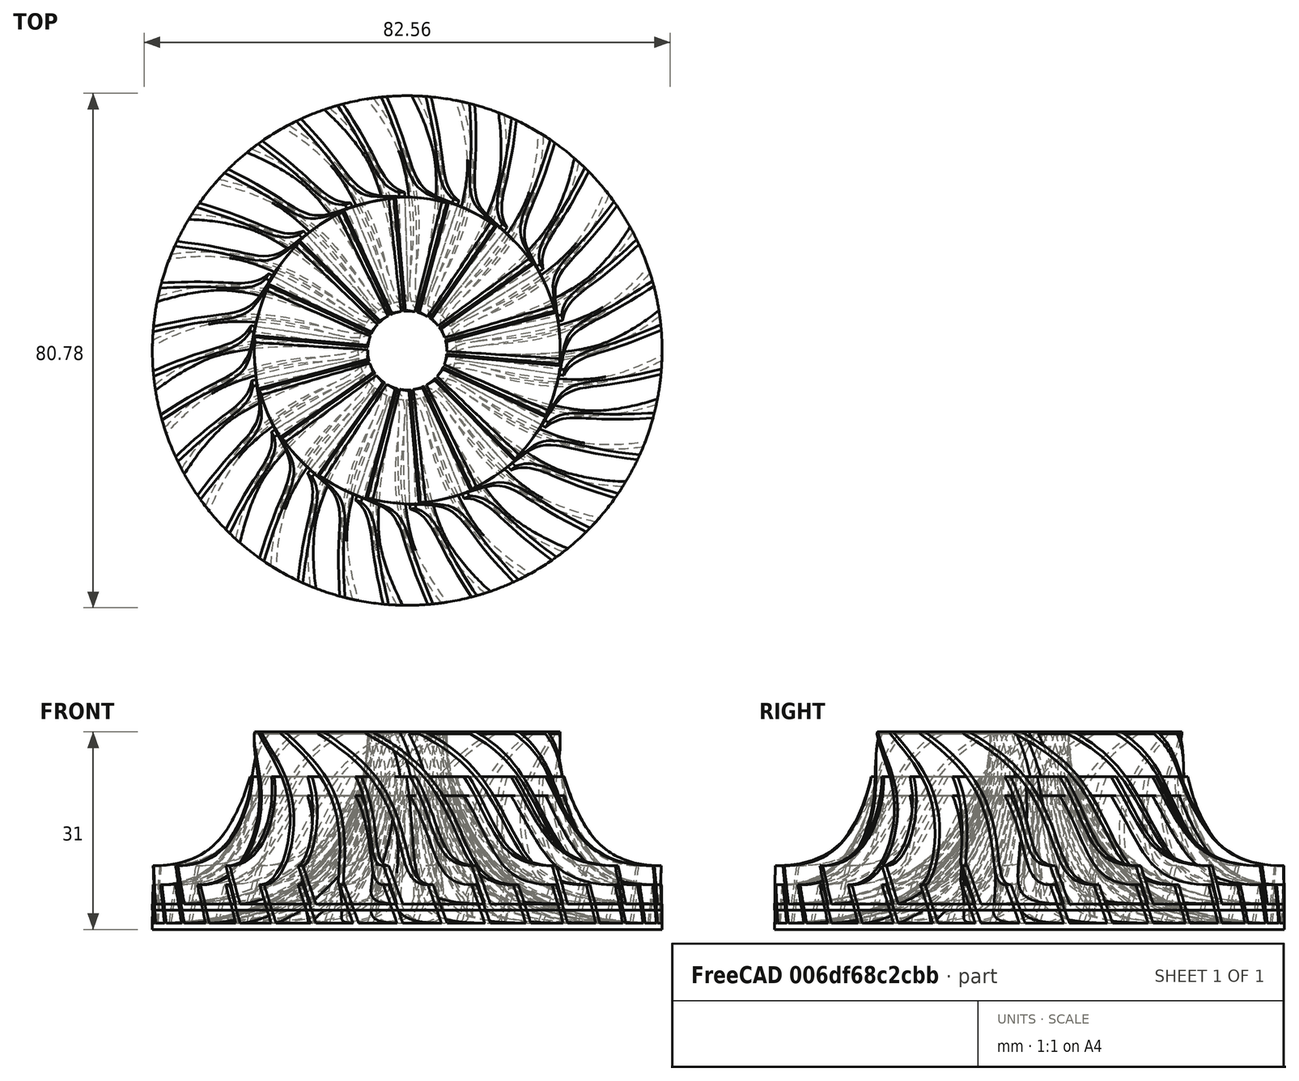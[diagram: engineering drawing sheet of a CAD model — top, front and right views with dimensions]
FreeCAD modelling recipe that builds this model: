
FCSTD DOCUMENT  (FreeCAD 0.18R4 (GitTag))
Label: impeler
License: All rights reserved
LicenseURL: http://en.wikipedia.org/wiki/All_rights_reserved
objects: Sketcher::SketchObject×15, PartDesign::Plane×4, PartDesign::Groove×4, PartDesign::Pocket×3, PartDesign::AdditiveLoft×2, PartDesign::PolarPattern×2, PartDesign::Revolution×2, PartDesign::Body×2, PartDesign::Boolean×1
note: 46 computed .brp shape members not serialized (recipe doc carries the construction recipe); baked Part::Feature solids carry a one-line shape summary decoded from their .brp

FEATURE [PartDesign::Plane] DatumPlane006
  AttachmentOffset = pos=(0,0,20) rot=(0.702714,-0.111299,-0.702714;0.443371rad)
  Length = 121.396
  MapMode = 5
  Placement = pos=(0,0,20) rot=(0.702714,-0.111299,-0.702714;0.443371rad)
  ResizeMode = 0
  Support = -> [XY_Plane007]
  Width = 125.733
FEATURE [PartDesign::Plane] DatumPlane007
  AttachmentOffset = pos=(0,0,30) rot=(0.678598,-0.281085,-0.678598;1.09606rad)
  Length = 134.539
  MapMode = 5
  Placement = pos=(0,0,30) rot=(0.678598,-0.281085,-0.678598;1.09606rad)
  ResizeMode = 0
  Support = -> [XY_Plane007]
  Width = 122.615
FEATURE [Sketcher::SketchObject] Sketch042  label="Sketch043"
  MapMode = 5
  Placement = pos=(0,0,0) rot=(1,0,0;1.5708rad)
  Support = -> [XZ_Plane004]
  sketch-geometry (13):
    g0: LineSegment StartX=40 StartY=0 StartZ=0 EndX=40 EndY=-1 EndZ=0
    g1: LineSegment StartX=40 StartY=-1 StartZ=0 EndX=0 EndY=-1 EndZ=0
    g2: LineSegment StartX=0 StartY=-1 StartZ=0 EndX=0 EndY=30 EndZ=0
    g3: LineSegment StartX=0 StartY=30 StartZ=0 EndX=6.2 EndY=30 EndZ=0
    g4-g8: Circle [constr] x5 (B-spline internal-alignment scaffolding for g9; pole/knot coordinates omitted)
    g9: BSplineCurve PolesCount=5 KnotsCount=3 Degree=3 IsPeriodic=0
    g10: GeomPoint [constr] X=6.2 Y=30 Z=0
    g11: GeomPoint [constr] X=14.55 Y=8.5 Z=0
    g12: GeomPoint [constr] X=40 Y=0 Z=0
  constraints (27):
    c: PointOnObject(g0,g-1)
    c: Vertical(g0)
    c: Coincident(g0,g1)
    c: Horizontal(g1)
    c: Coincident(g1,g2)
    c: PointOnObject(g2,g-2)
    c: Vertical(g2)
    c: Coincident(g2,g3)
    c: Horizontal(g3)
    c: Distance(g1) = 40
    c: Distance(g0) = 1
    c: Distance(g-1,g2) = 30
    c: Coincident(g9,g3)
    c: Radius(g4) = 1
    c: Equal(g4, g5-g8) x4
    c: Coincident(g9,g0)
    c: InternalAlignment(g4-g8 -> g9) x5
    c: InternalAlignment(g10,g9)
    c: InternalAlignment(g11,g9)
    c: InternalAlignment(g12,g9)
    c: Horizontal(g7,g0)
    c: Vertical(g5,g3)
    c: Distance(g3) = 6.2
    c: DistanceY(g5,g3) = 8
    c: DistanceX(g7,g0) = 12
    c: DistanceX(g6,g7) = 16
    c: DistanceY(g6,g5) = 16
FEATURE [PartDesign::Plane] DatumPlane008
  AttachmentOffset = pos=(0,0,30) rot=(0.678598,-0.281085,-0.678598;1.09606rad)
  Length = 135.269
  MapMode = 5
  Placement = pos=(0,0,30) rot=(0.678598,-0.281085,-0.678598;1.09606rad)
  ResizeMode = 0
  Support = -> [XY_Plane008]
  Width = 130.418
FEATURE [PartDesign::Plane] DatumPlane009
  AttachmentOffset = pos=(0,0,20) rot=(0.702714,-0.111299,-0.702714;0.443371rad)
  Length = 121.693
  MapMode = 5
  Placement = pos=(0,0,20) rot=(0.702714,-0.111299,-0.702714;0.443371rad)
  ResizeMode = 0
  Support = -> [XY_Plane008]
  Width = 129.119
FEATURE [Sketcher::SketchObject] Sketch019
  MapMode = 5
  Placement = pos=(0,0,0) rot=(1,0,0;1.5708rad)
  Support = -> [XZ_Plane001]
  sketch-geometry (13):
    g0: LineSegment StartX=40 StartY=0 StartZ=0 EndX=40 EndY=-1 EndZ=0
    g1: LineSegment StartX=40 StartY=-1 StartZ=0 EndX=0 EndY=-1 EndZ=0
    g2: LineSegment StartX=0 StartY=-1 StartZ=0 EndX=0 EndY=30 EndZ=0
    g3: LineSegment StartX=0 StartY=30 StartZ=0 EndX=6.2 EndY=30 EndZ=0
    g4-g8: Circle [constr] x5 (B-spline internal-alignment scaffolding for g9; pole/knot coordinates omitted)
    g9: BSplineCurve PolesCount=5 KnotsCount=3 Degree=3 IsPeriodic=0
    g10: GeomPoint [constr] X=6.2 Y=30 Z=0
    g11: GeomPoint [constr] X=14.55 Y=8.5 Z=0
    g12: GeomPoint [constr] X=40 Y=0 Z=0
  constraints (27):
    c: PointOnObject(g0,g-1)
    c: Vertical(g0)
    c: Coincident(g0,g1)
    c: Horizontal(g1)
    c: Coincident(g1,g2)
    c: PointOnObject(g2,g-2)
    c: Vertical(g2)
    c: Coincident(g2,g3)
    c: Horizontal(g3)
    c: Distance(g1) = 40
    c: Distance(g0) = 1
    c: Distance(g-1,g2) = 30
    c: Coincident(g9,g3)
    c: Radius(g4) = 1
    c: Equal(g4, g5-g8) x4
    c: Coincident(g9,g0)
    c: InternalAlignment(g4-g8 -> g9) x5
    c: InternalAlignment(g10,g9)
    c: InternalAlignment(g11,g9)
    c: InternalAlignment(g12,g9)
    c: Horizontal(g7,g0)
    c: Vertical(g5,g3)
    c: Distance(g3) = 6.2
    c: DistanceY(g5,g3) = 8
    c: DistanceX(g7,g0) = 12
    c: DistanceX(g6,g7) = 16
    c: DistanceY(g6,g5) = 16
FEATURE [Sketcher::SketchObject] Sketch043  label="Sketch044"
  MapMode = 5
  Placement = pos=(0,0,0) rot=(1,0,0;1.5708rad)
  Support = -> [XZ_Plane004]
  sketch-geometry (13):
    g0-g4: Circle [constr] x5 (B-spline internal-alignment scaffolding for g5; pole/knot coordinates omitted)
    g5: BSplineCurve PolesCount=5 KnotsCount=3 Degree=3 IsPeriodic=0
    g6: GeomPoint [constr] X=24 Y=30 Z=0
    g7: GeomPoint [constr] X=27 Y=14 Z=0
    g8: GeomPoint [constr] X=40 Y=6 Z=0
    g9: LineSegment StartX=44 StartY=0 StartZ=0 EndX=44 EndY=30 EndZ=0
    g10: LineSegment StartX=44 StartY=30 StartZ=0 EndX=24 EndY=30 EndZ=0
    g11: LineSegment StartX=40 StartY=6 StartZ=0 EndX=40 EndY=0 EndZ=0
    g12: LineSegment StartX=40 StartY=0 StartZ=0 EndX=44 EndY=0 EndZ=0
  constraints (27):
    c: Radius(g0) = 1
    c: Equal(g0, g1-g4) x4
    c: InternalAlignment(g0-g4 -> g5) x5
    c: InternalAlignment(g6,g5)
    c: InternalAlignment(g7,g5)
    c: InternalAlignment(g8,g5)
    c: Vertical(g5,g1)
    c: Horizontal(g3,g5)
    c: DistanceX(g-1,g5) = 40
    c: DistanceX(g-1,g5) = 24
    c: Vertical(g9)
    c: Coincident(g9,g10)
    c: Coincident(g10,g5)
    c: Horizontal(g10)
    c: DistanceY(g-1,g5) = 30
    c: DistanceX(g5,g9) = 4
    c: Coincident(g12,g11)
    c: Coincident(g12,g9)
    c: Horizontal(g12)
    c: Coincident(g11,g5)
    c: Distance(g11) = 6
    c: PointOnObject(g11,g-1)
    c: DistanceX(g3,g5) = 8
    c: DistanceY(g1,g5) = 8
    c: DistanceY(g2,g1) = 8
    c: DistanceX(g2,g3) = 6
    c: Vertical(g11)
FEATURE [Sketcher::SketchObject] Sketch044  label="Sketch046"
  MapMode = 5
  Placement = pos=(0,1.8e-15,30) rot=(0.678598,-0.281085,-0.678598;1.09606rad)
  Support = -> [DatumPlane008]
  sketch-geometry (5):
    g0: LineSegment StartX=1 StartY=0.4 StartZ=0 EndX=43 EndY=0.4 EndZ=0
    g1: LineSegment StartX=43 StartY=0.4 StartZ=0 EndX=43 EndY=-0.4 EndZ=0
    g2: LineSegment StartX=43 StartY=-0.4 StartZ=0 EndX=1 EndY=-0.4 EndZ=0
    g3: LineSegment StartX=1 StartY=-0.4 StartZ=0 EndX=1 EndY=0.4 EndZ=0
    g4: GeomPoint X=1 Y=0 Z=0
  constraints (13):
    c: Horizontal(g0)
    c: Coincident(g0,g1)
    c: Vertical(g1)
    c: Coincident(g1,g2)
    c: Horizontal(g2)
    c: Coincident(g2,g3)
    c: Coincident(g3,g0)
    c: Distance(g0) = 42
    c: Distance(g1) = 0.8
    c: Vertical(g3)
    c: PointOnObject(g4,g-1)
    c: Symmetric(g2,g0,g4)
    c: DistanceX(g-1,g4) = 1
FEATURE [Sketcher::SketchObject] Sketch045  label="Sketch047"
  MapMode = 5
  Support = -> [XY_Plane008]
  sketch-geometry (8):
    g0: ArcOfCircle CenterX=21.5 CenterY=33.8808 CenterZ=0 NormalX=0 NormalY=0 NormalZ=1 AngleXU=0 Radius=40 StartAngle=4.16826 EndAngle=5.25652
    g1: GeomPoint X=42 Y=0 Z=0
    g2: LineSegment StartX=0.792929 StartY=-0.342231 StartZ=0 EndX=1.20707 EndY=0.342231 EndZ=0
    g3: LineSegment [constr] StartX=0.792929 StartY=-0.342231 StartZ=0 EndX=-8.03408 EndY=4.99866 EndZ=0
    g4: ArcOfCircle CenterX=21.5 CenterY=33.8808 CenterZ=0 NormalX=0 NormalY=0 NormalZ=1 AngleXU=0 Radius=39.2 StartAngle=4.16826 EndAngle=5.25652
    g5: LineSegment StartX=41.7929 StartY=0.342231 StartZ=0 EndX=42.2071 EndY=-0.342231 EndZ=0
    g6: LineSegment [constr] StartX=42.2071 StartY=-0.342231 StartZ=0 EndX=44.6326 EndY=1.12535 EndZ=0
    g7: GeomPoint X=1 Y=0 Z=0
  constraints (17):
    c: Radius(g0) = 40
    c: DistanceX(g-1,g1) = 42
    c: Coincident(g2,g0)
    c: Tangent(g3,g0) = 1.5708
    c: Perpendicular(g3,g2)
    c: Coincident(g4,g0)
    c: Coincident(g5,g0)
    c: PointOnObject(g1,g-1)
    c: Coincident(g4,g2)
    c: Coincident(g4,g5)
    c: Distance(g2) = 0.8
    c: Symmetric(g0,g4,g1)
    c: Tangent(g6,g0) = -1.5708
    c: Perpendicular(g5,g6)
    c: PointOnObject(g7,g-1)
    c: Symmetric(g0,g2,g7)
    c: DistanceX(g-1,g7) = 1
FEATURE [Sketcher::SketchObject] Sketch016
  MapMode = 5
  Placement = pos=(0,0,0) rot=(1,0,0;1.5708rad)
  Support = -> [XZ_Plane004]
  sketch-geometry (10):
    g0: LineSegment StartX=0 StartY=-1 StartZ=0 EndX=13 EndY=-1 EndZ=0
    g1: LineSegment StartX=13 StartY=-1 StartZ=0 EndX=13 EndY=2 EndZ=0
    g2: LineSegment StartX=11.5 StartY=3.5 StartZ=0 EndX=11.5 EndY=8 EndZ=0
    g3: LineSegment StartX=11.5 StartY=8 StartZ=0 EndX=3 EndY=8 EndZ=0
    g4: LineSegment StartX=3 StartY=8 StartZ=0 EndX=3 EndY=12 EndZ=0
    g5: LineSegment StartX=3 StartY=12 StartZ=0 EndX=5 EndY=12 EndZ=0
    g6: LineSegment StartX=5 StartY=12 StartZ=0 EndX=5 EndY=30 EndZ=0
    g7: LineSegment StartX=5 StartY=30 StartZ=0 EndX=0 EndY=30 EndZ=0
    g8: LineSegment StartX=0 StartY=30 StartZ=0 EndX=0 EndY=-1 EndZ=0
    g9: LineSegment StartX=13 StartY=2 StartZ=0 EndX=11.5 EndY=3.5 EndZ=0
  constraints (30):
    c: PointOnObject(g0,g-2)
    c: Horizontal(g0)
    c: Coincident(g0,g1)
    c: Vertical(g2)
    c: Coincident(g2,g3)
    c: Horizontal(g3)
    c: Coincident(g3,g4)
    c: Vertical(g4)
    c: Coincident(g4,g5)
    c: Horizontal(g5)
    c: Coincident(g5,g6)
    c: Vertical(g6)
    c: Coincident(g6,g7)
    c: PointOnObject(g7,g-2)
    c: Horizontal(g7)
    c: Coincident(g7,g8)
    c: Coincident(g8,g0)
    c: Vertical(g1)
    c: Distance(g0) = 13
    c: Distance(g1) = 3
    c: Distance(g0,g-1) = 1
    c: Distance(g2,g0) = 9
    c: Distance(g4) = 4
    c: Distance(g3,g8) = 3
    c: Distance(g5,g8) = 5
    c: Distance(g7,g-1) = 30
    c: Distance(g2,g8) = 11.5
    c: Coincident(g9,g1)
    c: Coincident(g2,g9)
    c: Angle(g9,g0) = 0.785398
FEATURE [Sketcher::SketchObject] Sketch046  label="Sketch048"
  MapMode = 5
  Placement = pos=(-2e-16,0,20) rot=(0.702714,-0.111299,-0.702714;0.443371rad)
  Support = -> [DatumPlane009]
  sketch-geometry (5):
    g0: LineSegment StartX=1 StartY=0.4 StartZ=0 EndX=43 EndY=0.4 EndZ=0
    g1: LineSegment StartX=43 StartY=0.4 StartZ=0 EndX=43 EndY=-0.4 EndZ=0
    g2: LineSegment StartX=43 StartY=-0.4 StartZ=0 EndX=1 EndY=-0.4 EndZ=0
    g3: LineSegment StartX=1 StartY=-0.4 StartZ=0 EndX=1 EndY=0.4 EndZ=0
    g4: GeomPoint X=1 Y=0 Z=0
  constraints (13):
    c: Horizontal(g0)
    c: Coincident(g0,g1)
    c: Vertical(g1)
    c: Coincident(g1,g2)
    c: Horizontal(g2)
    c: Coincident(g2,g3)
    c: Coincident(g3,g0)
    c: Distance(g1) = 0.8
    c: Distance(g0) = 42
    c: Vertical(g3)
    c: PointOnObject(g4,g-1)
    c: Symmetric(g2,g0,g4)
    c: DistanceX(g-1,g4) = 1
FEATURE [PartDesign::AdditiveLoft] AdditiveLoft
  Closed = false
  Profile = -> Sketch045
  Ruled = false
  Sections = -> [Sketch045,Sketch046,Sketch044]
FEATURE [PartDesign::PolarPattern] PolarPattern
  Angle = 360
  Axis = -> Sketch045 [N_Axis]
  BaseFeature = -> AdditiveLoft
  Occurrences = 18
  Originals = -> [AdditiveLoft]
FEATURE [PartDesign::Revolution] Revolution005
  Angle = 360
  Axis = (-3e-16,3e-16,1)
  Base = (0,0,0)
  BaseFeature = -> PolarPattern
  Profile = -> Sketch042
  ReferenceAxis = -> Z_Axis004
  Reversed = true
FEATURE [PartDesign::Groove] Groove
  Angle = 360
  Axis = (-3e-16,3e-16,1)
  Base = (0,0,0)
  BaseFeature = -> Revolution005
  Profile = -> Sketch043
  ReferenceAxis = -> Z_Axis004
FEATURE [Sketcher::SketchObject] Sketch020
  MapMode = 5
  Placement = pos=(0,0,0) rot=(1,0,0;1.5708rad)
  Support = -> [XZ_Plane001]
  sketch-geometry (13):
    g0-g4: Circle [constr] x5 (B-spline internal-alignment scaffolding for g5; pole/knot coordinates omitted)
    g5: BSplineCurve PolesCount=5 KnotsCount=3 Degree=3 IsPeriodic=0
    g6: GeomPoint [constr] X=24 Y=30 Z=0
    g7: GeomPoint [constr] X=27 Y=14 Z=0
    g8: GeomPoint [constr] X=40 Y=6 Z=0
    g9: LineSegment StartX=44 StartY=0 StartZ=0 EndX=44 EndY=30 EndZ=0
    g10: LineSegment StartX=44 StartY=30 StartZ=0 EndX=24 EndY=30 EndZ=0
    g11: LineSegment StartX=40 StartY=6 StartZ=0 EndX=40 EndY=0 EndZ=0
    g12: LineSegment StartX=40 StartY=0 StartZ=0 EndX=44 EndY=0 EndZ=0
  constraints (27):
    c: Radius(g0) = 1
    c: Equal(g0, g1-g4) x4
    c: InternalAlignment(g0-g4 -> g5) x5
    c: InternalAlignment(g6,g5)
    c: InternalAlignment(g7,g5)
    c: InternalAlignment(g8,g5)
    c: Vertical(g5,g1)
    c: Horizontal(g3,g5)
    c: DistanceX(g-1,g5) = 40
    c: DistanceX(g-1,g5) = 24
    c: Vertical(g9)
    c: Coincident(g9,g10)
    c: Coincident(g10,g5)
    c: Horizontal(g10)
    c: DistanceY(g-1,g5) = 30
    c: DistanceX(g5,g9) = 4
    c: Coincident(g12,g11)
    c: Coincident(g12,g9)
    c: Horizontal(g12)
    c: Coincident(g11,g5)
    c: Distance(g11) = 6
    c: PointOnObject(g11,g-1)
    c: DistanceX(g3,g5) = 8
    c: DistanceY(g1,g5) = 8
    c: DistanceY(g2,g1) = 8
    c: DistanceX(g2,g3) = 6
    c: Vertical(g11)
FEATURE [Sketcher::SketchObject] Sketch021  label="Sketch022"
  MapMode = 5
  Placement = pos=(0,1.8e-15,30) rot=(0.678598,-0.281085,-0.678598;1.09606rad)
  Support = -> [DatumPlane007]
  sketch-geometry (5):
    g0: LineSegment StartX=1 StartY=0.4 StartZ=0 EndX=43 EndY=0.4 EndZ=0
    g1: LineSegment StartX=43 StartY=0.4 StartZ=0 EndX=43 EndY=-0.4 EndZ=0
    g2: LineSegment StartX=43 StartY=-0.4 StartZ=0 EndX=1 EndY=-0.4 EndZ=0
    g3: LineSegment StartX=1 StartY=-0.4 StartZ=0 EndX=1 EndY=0.4 EndZ=0
    g4: GeomPoint X=1 Y=0 Z=0
  constraints (13):
    c: Horizontal(g0)
    c: Coincident(g0,g1)
    c: Vertical(g1)
    c: Coincident(g1,g2)
    c: Horizontal(g2)
    c: Coincident(g2,g3)
    c: Coincident(g3,g0)
    c: Distance(g0) = 42
    c: Distance(g1) = 0.8
    c: Vertical(g3)
    c: PointOnObject(g4,g-1)
    c: Symmetric(g2,g0,g4)
    c: DistanceX(g-1,g4) = 1
FEATURE [Sketcher::SketchObject] Sketch022  label="Sketch023"
  MapMode = 5
  Placement = pos=(-2e-16,0,20) rot=(0.702714,-0.111299,-0.702714;0.443371rad)
  Support = -> [DatumPlane006]
  sketch-geometry (5):
    g0: LineSegment StartX=1 StartY=0.4 StartZ=0 EndX=43 EndY=0.4 EndZ=0
    g1: LineSegment StartX=43 StartY=0.4 StartZ=0 EndX=43 EndY=-0.4 EndZ=0
    g2: LineSegment StartX=43 StartY=-0.4 StartZ=0 EndX=1 EndY=-0.4 EndZ=0
    g3: LineSegment StartX=1 StartY=-0.4 StartZ=0 EndX=1 EndY=0.4 EndZ=0
    g4: GeomPoint X=1 Y=0 Z=0
  constraints (13):
    c: Horizontal(g0)
    c: Coincident(g0,g1)
    c: Vertical(g1)
    c: Coincident(g1,g2)
    c: Horizontal(g2)
    c: Coincident(g2,g3)
    c: Coincident(g3,g0)
    c: Distance(g1) = 0.8
    c: Distance(g0) = 42
    c: Vertical(g3)
    c: PointOnObject(g4,g-1)
    c: Symmetric(g2,g0,g4)
    c: DistanceX(g-1,g4) = 1
FEATURE [Sketcher::SketchObject] Sketch023  label="Sketch024"
  MapMode = 5
  Support = -> [XY_Plane007]
  sketch-geometry (8):
    g0: ArcOfCircle CenterX=21.5 CenterY=33.8808 CenterZ=0 NormalX=0 NormalY=0 NormalZ=1 AngleXU=0 Radius=40 StartAngle=4.16826 EndAngle=5.25652
    g1: GeomPoint X=42 Y=0 Z=0
    g2: LineSegment StartX=0.792929 StartY=-0.342231 StartZ=0 EndX=1.20707 EndY=0.342231 EndZ=0
    g3: LineSegment [constr] StartX=0.792929 StartY=-0.342231 StartZ=0 EndX=-8.03408 EndY=4.99866 EndZ=0
    g4: ArcOfCircle CenterX=21.5 CenterY=33.8808 CenterZ=0 NormalX=0 NormalY=0 NormalZ=1 AngleXU=0 Radius=39.2 StartAngle=4.16826 EndAngle=5.25652
    g5: LineSegment StartX=41.7929 StartY=0.342231 StartZ=0 EndX=42.2071 EndY=-0.342231 EndZ=0
    g6: LineSegment [constr] StartX=42.2071 StartY=-0.342231 StartZ=0 EndX=44.6326 EndY=1.12535 EndZ=0
    g7: GeomPoint X=1 Y=0 Z=0
  constraints (17):
    c: Radius(g0) = 40
    c: DistanceX(g-1,g1) = 42
    c: Coincident(g2,g0)
    c: Tangent(g3,g0) = 1.5708
    c: Perpendicular(g3,g2)
    c: Coincident(g4,g0)
    c: Coincident(g5,g0)
    c: PointOnObject(g1,g-1)
    c: Coincident(g4,g2)
    c: Coincident(g4,g5)
    c: Distance(g2) = 0.8
    c: Symmetric(g0,g4,g1)
    c: Tangent(g6,g0) = -1.5708
    c: Perpendicular(g5,g6)
    c: PointOnObject(g7,g-1)
    c: Symmetric(g0,g2,g7)
    c: DistanceX(g-1,g7) = 1
FEATURE [PartDesign::AdditiveLoft] AdditiveLoft001
  Closed = false
  Profile = -> Sketch023
  Ruled = false
  Sections = -> [Sketch023,Sketch022,Sketch021]
FEATURE [PartDesign::PolarPattern] PolarPattern001
  Angle = 360
  Axis = -> Sketch023 [N_Axis]
  BaseFeature = -> AdditiveLoft001
  Occurrences = 18
  Originals = -> [AdditiveLoft001]
FEATURE [PartDesign::Revolution] Revolution006
  Angle = 360
  Axis = (-3e-16,3e-16,1)
  Base = (0,0,0)
  BaseFeature = -> PolarPattern001
  Profile = -> Sketch019
  ReferenceAxis = -> Z_Axis001
  Reversed = true
FEATURE [PartDesign::Groove] Groove003
  Angle = 360
  Axis = (-3e-16,3e-16,1)
  Base = (0,0,0)
  BaseFeature = -> Revolution006
  Profile = -> Sketch020
  ReferenceAxis = -> Z_Axis001
FEATURE [Sketcher::SketchObject] Sketch024  label="Sketch049"
  MapMode = 5
  Placement = pos=(0,0,0) rot=(1,0,0;1.5708rad)
  Support = -> [XZ_Plane001]
  sketch-geometry (10):
    g0: LineSegment StartX=0 StartY=-1 StartZ=0 EndX=13 EndY=-1 EndZ=0
    g1: LineSegment StartX=13 StartY=-1 StartZ=0 EndX=13 EndY=2 EndZ=0
    g2: LineSegment StartX=11.5 StartY=3.5 StartZ=0 EndX=11.5 EndY=8 EndZ=0
    g3: LineSegment StartX=11.5 StartY=8 StartZ=0 EndX=3 EndY=8 EndZ=0
    g4: LineSegment StartX=3 StartY=8 StartZ=0 EndX=3 EndY=12 EndZ=0
    g5: LineSegment StartX=3 StartY=12 StartZ=0 EndX=5 EndY=12 EndZ=0
    g6: LineSegment StartX=5 StartY=12 StartZ=0 EndX=5 EndY=30 EndZ=0
    g7: LineSegment StartX=5 StartY=30 StartZ=0 EndX=0 EndY=30 EndZ=0
    g8: LineSegment StartX=0 StartY=30 StartZ=0 EndX=0 EndY=-1 EndZ=0
    g9: LineSegment StartX=13 StartY=2 StartZ=0 EndX=11.5 EndY=3.5 EndZ=0
  constraints (30):
    c: PointOnObject(g0,g-2)
    c: Horizontal(g0)
    c: Coincident(g0,g1)
    c: Vertical(g2)
    c: Coincident(g2,g3)
    c: Horizontal(g3)
    c: Coincident(g3,g4)
    c: Vertical(g4)
    c: Coincident(g4,g5)
    c: Horizontal(g5)
    c: Coincident(g5,g6)
    c: Vertical(g6)
    c: Coincident(g6,g7)
    c: PointOnObject(g7,g-2)
    c: Horizontal(g7)
    c: Coincident(g7,g8)
    c: Coincident(g8,g0)
    c: Vertical(g1)
    c: Distance(g0) = 13
    c: Distance(g1) = 3
    c: Distance(g0,g-1) = 1
    c: Distance(g2,g0) = 9
    c: Distance(g4) = 4
    c: Distance(g3,g8) = 3
    c: Distance(g5,g8) = 5
    c: Distance(g7,g-1) = 30
    c: Distance(g2,g8) = 11.5
    c: Coincident(g9,g1)
    c: Coincident(g2,g9)
    c: Angle(g9,g0) = 0.785398
FEATURE [PartDesign::Pocket] Pocket007
  BaseFeature = -> Pocket001
  Length = 10
  Length2 = 100
  Profile = -> Sketch047
  Type = 0
FEATURE [PartDesign::Groove] Groove004
  Angle = 360
  Axis = (-3e-16,3e-16,1)
  Base = (0,0,0)
  BaseFeature = -> Pocket007
  Profile = -> Sketch024
  ReferenceAxis = -> Z_Axis001
  Refine = true
FEATURE [PartDesign::Boolean] Boolean
  BaseFeature = -> Pocket008
  Group = -> [Body001]
  Type = 0
FEATURE [PartDesign::Pocket] Pocket001
  BaseFeature = -> Groove003
  Length = 5
  Length2 = 100
  Profile = -> Sketch018
  Reversed = true
  Type = 1
FEATURE [PartDesign::Groove] Groove002
  Angle = 360
  Axis = (-3e-16,3e-16,1)
  Base = (0,0,0)
  BaseFeature = -> Boolean
  Profile = -> Sketch016
  ReferenceAxis = -> Z_Axis004
  Refine = true
FEATURE [PartDesign::Pocket] Pocket008
  BaseFeature = -> Groove
  Length = 5
  Length2 = 100
  Profile = -> Sketch017
  Reversed = true
  Type = 1
FEATURE [PartDesign::Body] Body001
  Group = -> [Sketch023,DatumPlane006,Sketch022,DatumPlane007,Sketch021,Sketch019,AdditiveLoft001,PolarPattern001,Revolution006,Sketch020,Groove003,Sketch024,Sketch018,Pocket001,Sketch047,Pocket007,Groove004]
  Origin = -> Origin001
  Placement = pos=(0,0,0) rot=(0,0,1;0.174533rad)
  Tip = -> Pocket007
FEATURE [PartDesign::Body] Body004  label="impeller"
  Group = -> [Sketch045,DatumPlane009,Sketch046,DatumPlane008,Sketch044,Sketch042,AdditiveLoft,PolarPattern,Revolution005,Sketch043,Groove,Sketch016,Sketch017,Pocket008,Boolean,Groove002]
  Origin = -> Origin004
  Placement = pos=(0,0,-3) rot=(0,0,1;0rad)
  Tip = -> Boolean
FEATURE [Sketcher::SketchObject] Sketch017
  MapMode = 5
  Placement = pos=(-1e-14,1e-14,30) rot=(0,0,1;0rad)
  Support = -> [Groove002]
  sketch-geometry (1):
    g0: Circle CenterX=0 CenterY=0 CenterZ=0 NormalX=0 NormalY=0 NormalZ=1 AngleXU=0 Radius=54.919
  constraints (1):
    c: Coincident(g0,g-1)
FEATURE [Sketcher::SketchObject] Sketch018
  MapMode = 5
  Placement = pos=(-1e-14,1e-14,30) rot=(0,0,1;0rad)
  Support = -> [Groove004]
  sketch-geometry (1):
    g0: Circle CenterX=0 CenterY=0 CenterZ=0 NormalX=0 NormalY=0 NormalZ=1 AngleXU=0 Radius=54.919
  constraints (1):
    c: Coincident(g0,g-1)
FEATURE [Sketcher::SketchObject] Sketch047  label="Sketch026"
  MapMode = 5
  Placement = pos=(-1e-14,1e-14,30) rot=(0,0,1;0rad)
  Support = -> [Groove004]
  sketch-geometry (1):
    g0: Circle CenterX=0 CenterY=0 CenterZ=0 NormalX=0 NormalY=0 NormalZ=1 AngleXU=0 Radius=50
  constraints (2):
    c: Coincident(g0,g-1)
    c: Radius(g0) = 50
